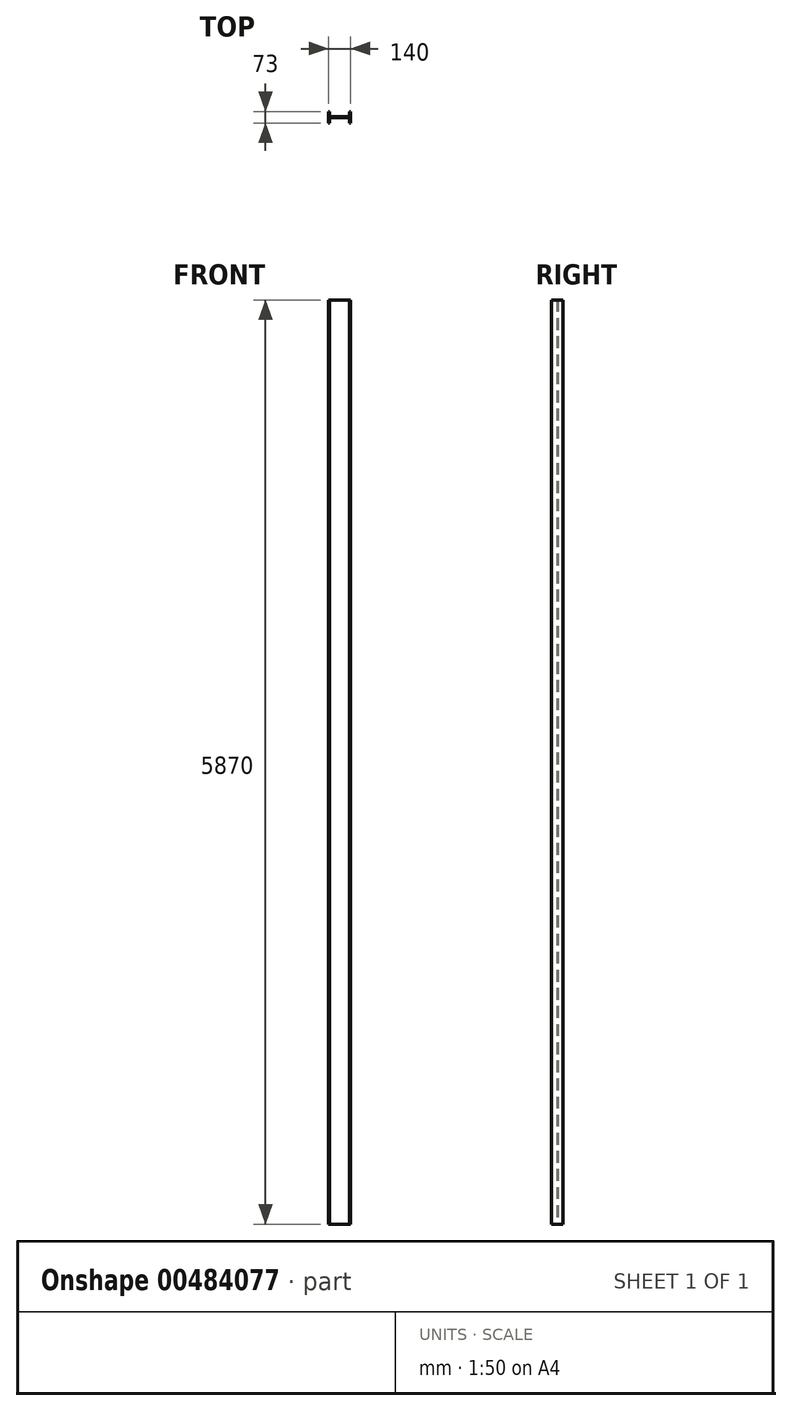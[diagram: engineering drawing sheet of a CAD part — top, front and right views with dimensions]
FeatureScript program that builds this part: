
annotation { "Feature Type Name" : "Feature", "Feature Type Description" : "" }
export const myFeature = defineFeature(function(context is Context, id is Id, definition is map)
    precondition{}
    {
        {
            var Q0;
            Q0=qCreatedBy(makeId("Top.planeOp"),FACE);
            var sketch = newSketch(context, id + "F0", { "sketchPlane" : qUnion([Q0])});
            skLineSegment(sketch, "E0", {"start": v(-140, 0) * mm, "end": v(-140, 73) * mm});
            skLineSegment(sketch, "E1", {"start": v(-140, 73) * mm, "end": v(-133.1, 73) * mm});
            skLineSegment(sketch, "E2", {"start": v(-133.1, 73) * mm, "end": v(-133.1, 43.85) * mm});
            skLineSegment(sketch, "E3", {"start": v(-128.1, 38.85) * mm, "end": v(-11.9, 38.85) * mm});
            skLineSegment(sketch, "E4", {"start": v(-6.9, 43.85) * mm, "end": v(-6.9, 73) * mm});
            skLineSegment(sketch, "E5", {"start": v(-6.9, 73) * mm, "end": v(0, 73) * mm});
            skLineSegment(sketch, "E6", {"start": v(0, 73) * mm, "end": v(0, 0) * mm});
            skLineSegment(sketch, "E7", {"start": v(0, 0) * mm, "end": v(-6.9, 0) * mm});
            skLineSegment(sketch, "E8", {"start": v(-6.9, 0) * mm, "end": v(-6.9, 29.15) * mm});
            skLineSegment(sketch, "E9", {"start": v(-11.9, 34.15) * mm, "end": v(-128.1, 34.15) * mm});
            skLineSegment(sketch, "E10", {"start": v(-133.1, 29.15) * mm, "end": v(-133.1, 0) * mm});
            skLineSegment(sketch, "E11", {"start": v(-133.1, 0) * mm, "end": v(-140, 0) * mm});
            skPoint(sketch, "E12.visualSharp", {"position": v(-133.1, 34.15) * mm});
            skArc(sketch, "E12.filletArc", {"start": v(-128.1, 34.15) * mm, "mid": v(-131.64, 32.69) * mm, "end": v(-133.1, 29.15) * mm});
            skPoint(sketch, "E13.visualSharp", {"position": v(-133.1, 38.85) * mm});
            skArc(sketch, "E13.filletArc", {"start": v(-133.1, 43.85) * mm, "mid": v(-131.64, 40.31) * mm, "end": v(-128.1, 38.85) * mm});
            skPoint(sketch, "E14.visualSharp", {"position": v(-6.9, 34.15) * mm});
            skArc(sketch, "E14.filletArc", {"start": v(-6.9, 29.15) * mm, "mid": v(-8.36, 32.69) * mm, "end": v(-11.9, 34.15) * mm});
            skPoint(sketch, "E15.visualSharp", {"position": v(-6.9, 38.85) * mm});
            skArc(sketch, "E15.filletArc", {"start": v(-11.9, 38.85) * mm, "mid": v(-8.36, 40.31) * mm, "end": v(-6.9, 43.85) * mm});
            skSolve(sketch);
        }
        {
            var Q0;
            Q0 = qSketchRegion(id + "F0", true);
            extrude(context, id + "F1", {"entities" : qUnion([Q0]), "depth" : 5870 * mm, "offsetDistance" : 25 * mm});
        }
    });
